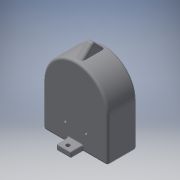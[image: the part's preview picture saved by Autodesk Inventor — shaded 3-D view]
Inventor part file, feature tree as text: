
AUTODESK INVENTOR PART (.ipt)
format: ipt  version: 2018 (Build 220112000, 112)  size: 281,600 bytes
history: native  units: in
note: dims shown in document units (in); Inventor stores cm internally (conversion verified against a paired STEP export)
features: extrude x7, sketch x6, fillet x5, reference x4, plane x1
ambient origin geometry x8: Origin, YZ Plane, XZ Plane, XY Plane, X Axis, Y Axis, Z Axis, Center Point
bodies: Solid1 (feature_tree)
feature tree (23):
  extrude  "Extrusion1"  Depth=0.4in TaperAngle=0.0deg
  extrude  "Extrusion2"  Depth=0.5in
  extrude  "Extrusion4"  Depth=0.4in TaperAngle=0.0deg
  extrude  "Extrusion5"  Depth=0.1378in
  extrude  "Extrusion6"  Depth=0.25in
  plane  "Work Plane1"
  extrude  "Extrusion7"  Depth=0.197in
  extrude  "Extrusion9"  Depth=0.15in
  fillet  "Fillet1"  Radius=0.1772in
  fillet  "Fillet2"  Radius=0.4in
  fillet  "Fillet3"  Radius=0.25in
  fillet  "Fillet4"  Radius=2.2in
  fillet  "Fillet5"  [1 undecoded]
  sketch  "Sketch1"  dims[d1=1.0in d2=0.0in d4=0.4in d5=0.0in]
  reference  "Reference1"
  sketch  "Sketch2"  dims[d10=0.25in d11=0.5in]
  reference  "Reference2"
  sketch  "Sketch5"  dims[d12=0.197in d13=0.4in d14=0.0in]
  sketch  "Sketch6"  dims[d15=0.15in d16=0.1378in]
  sketch  "Sketch7"  dims[d17=0.4in d18=0.0in d19=0.25in]
  sketch  "Sketch9"  dims[d20=0.5in d21=0.197in d22=0.15in d23=0.1772in d24=0.4in d25=0.0in d26=0.25in d27=2.2in d28=-1.1in d29=0.1065in d30=0.787in d31=0.394in d32=0.394in d33=0.25in d34=0.0in d41=0.0394in d42=0.0394in d43=0.098in d44=0.098in d45=1.0in d46=0.0in d47=0.0394in d48=0.0394in d49=0.0787in d50=0.0787in d51=0.0394in]
  reference  "Reference5"
  reference  "Reference6"
note: 1 required parameter value undecoded (feature->parameter linkage not recoverable at this tier; creation-order binding heuristic only, values carry confidence <= 0.55)
